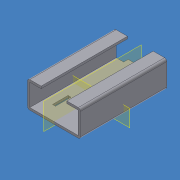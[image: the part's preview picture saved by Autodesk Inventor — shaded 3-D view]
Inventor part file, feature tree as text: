
AUTODESK INVENTOR PART (.ipt)
format: ipt  version: 2015 SP1 (Build 190203100, 203)  size: 224,768 bytes
history: native  units: mm
features: sheet_metal_op x9, other x8, sketch x6, plane x2
ambient origin geometry x8: Origin, YZ Plane, XZ Plane, XY Plane, X Axis, Y Axis, Z Axis, Center Point
bodies: Solid1 (feature_tree)
feature tree (25):
  sheet_metal_op  "Face1"
  sheet_metal_op  "Flange1"
  sheet_metal_op  "Flange2"
  sheet_metal_op  "Flange3"
  sheet_metal_op  "Flange4"
  plane  "Work Plane7"
  plane  "Work Plane6"
  sketch  "Sketch1"  dims[d4=0.001mm]
  other  "Plate1"
  sketch  "Sketch2"  dims[d5=3.0mm]
  other  "Plate2"
  sheet_metal_op  "Bend1"
  sketch  "Sketch3"  dims[d6=0.001mm]
  other  "Plate3"
  sheet_metal_op  "Bend2"
  sketch  "Sketch4"  dims[d7=6.0mm]
  other  "Plate4"
  sheet_metal_op  "Bend3"
  sketch  "Sketch5"  dims[d8=0.001mm]
  other  "Plate5"
  sheet_metal_op  "Bend4"
  sketch  "Sketch6"  dims[d9=29.0mm d10=90.0deg d11=0.001mm d12=3.0mm d13=0.001mm d14=6.0mm d15=0.001mm d16=29.0mm d17=90.0deg d18=0.001mm d19=3.0mm d20=0.001mm d21=6.0mm d22=0.001mm d23=15.0mm d24=90.0deg d25=0.001mm d26=3.0mm d27=0.001mm d28=6.0mm d29=0.001mm d30=15.0mm d31=90.0deg d32=0.001mm d33=4.0mm d34=20.5mm d35=4.0mm d36=20.5mm d37=0.0mm d38=33.0mm d40=4.0mm d41=0.0mm d42=114.0mm d46=9.0mm d47=0.0mm d48=4.0mm d49=10.0mm d50=10.0mm d51=6.0mm d52=64.0mm d53=64.0mm d56=18.5mm d0=3.0mm]
  other  "FlatPattern"
  other  "Cut1"
  other  "FlatPatternExtrusion2"
